# Revit family: bfs-300_1000tx2_50Hz
name_source: partatom
category: 機械設備
units: mm (PartAtom-declared; Revit-internal decimal feet)

## family parameters
OmniClass タイトル = Axial Fans
OmniClass 番号 = 23.75.35.17.24
パーツ タイプ = 割り込み
ロード時にボイドで切り取り = いいえ
丸型コネクタ寸法 = 直径を使用
作業面ベース = いいえ
共有 = いいえ
常に垂直 = はい
部屋計算ポイント = はい

## types (5) — shared parameters
IfcExportAs = IfcFanType
IfcExportType = CENTRIFUGALFORWARDCURVED
M = 80  [stored 0.262467 ft]
MID静圧 = 0.0 Pa
MID風量 = 0.0 m³/h
MIN静圧 = 0.0 Pa
MIN風量 = 0.0 m³/h
OmniClassCode = 23-33 31 19 13 15
URL = https://www.mitsubishielectric.co.jp
Uniclass2015Code = Pr_65_67_29_12
Uniclass2015Title = Centrifugal fans
Uniclass2015Version = Systems v1.9
サービススペース = はい
ドレン管径 = 18 mm
ファンの種類 = 多翼形
仕様書バージョン = Version1.0
企業コード = 108420
分類コード = 50052502100020
周波数 = 50 Hz
呼称 = 消音ボックス付送風機
実風量 = 0.0 m³/h
形名 = BFS-TX : BFS-300TX
本体マテリアル = SUS304
極 = 4
極数 = 3
法定耐用年数 = 15
盤工事区分 = 電気工事
相 = 3
積算_科目 = 2 換気設備
製品リリース年月 = 2022年6月1日
製品出荷対象 = 国内
製造元 = 三菱電機株式会社
設置方法 = 天吊
説明 = ストレートシロッコファン厨房用
負荷分類 = 3_ファン類
運転質量 = 0.00 kg
電圧 = 200 V
zero-valued in all types: Clearance Bottom, Clearance Right, Clearance Top

## per-type parameters (varying)
| type | Clearance Back | Clearance Front | Clearance Left | Depth | Front-d | Height | MAX静圧 | MAX風量 | Width | ダクト幅 | ダクト高 | 価格 | 天吊金具ピッチ奥行 | 天吊金具ピッチ幅 | 消費電力 | 番手 | 製品質量 | 質量 | 電動機出力 | 騒音レベル(dB(A)) | 騒音レベル(dB(A))_側面 | 騒音レベル(dB(A))_吐出 | 騒音レベル(dB(A))_吸込 |
| BFS-300TX2 | 0  [stored 0 ft] | 0  [stored 0 ft] | 600  [stored 1.9685 ft] | 614  [stored 2.01444 ft] | 80  [stored 0.262467 ft] | 411  [stored 1.34843 ft] | 200.0 Pa | 3000.0 m³/h | 546  [stored 1.79134 ft] | 300 mm | 300 mm | 463000 $ | 562  [stored 1.84383 ft] | 655  [stored 2.14895 ft] | 940 W | #2 | 39.00 kg | 46.80 kg | 1500 W | 68 | 49 | 73 | 68 |
| BFS-450TX2 | 600  [stored 1.9685 ft] | 600  [stored 1.9685 ft] | 1200 | 728  [stored 2.38845 ft] | 81.5  [stored 0.267388 ft] | 415  [stored 1.36155 ft] | 190.0 Pa | 4500.0 m³/h | 819  [stored 2.68701 ft] | 700 mm | 250 mm | 745000 $ | 685 | 922  [stored 3.02493 ft] | 1030 W | #1 1/2×2 | 77.00 kg | 92.40 kg | 2200 W | 63 | 46 | 71 | 63 |
| BFS-550TX2 | 600  [stored 1.9685 ft] | 600  [stored 1.9685 ft] | 1200 | 771  [stored 2.52953 ft] | 81.5  [stored 0.267388 ft] | 455 | 200.0 Pa | 5500.0 m³/h | 912  [stored 2.99213 ft] | 750 mm | 300 mm | 830000 $ | 728  [stored 2.38845 ft] | 1015  [stored 3.33005 ft] | 1660 W | #2×2 | 84.00 kg | 100.80 kg | 3000 W | 68 | 49 | 71 | 68 |
| BFS-800TX2 | 18  [stored 0.0590551 ft] | 18  [stored 0.0590551 ft] | 1100 | 1690  [stored 5.54462 ft] | 18  [stored 0.0590551 ft] | 461.4  [stored 1.51378 ft] | 200.0 Pa | 8000.0 m³/h | 952  [stored 3.12336 ft] | 800 mm | 300 mm | 1980000 $ | 1630  [stored 5.34777 ft] | 1018  [stored 3.3399 ft] | 2600 W | #2×3 | 121.00 kg | 145.20 kg | 3500 W | 68 | 48.5 | 70.5 | 68 |
| BFS-1000TX2 | 18  [stored 0.0590551 ft] | 18  [stored 0.0590551 ft] | 1100 | 1910  [stored 6.2664 ft] | 18  [stored 0.0590551 ft] | 461.4  [stored 1.51378 ft] | 205.0 Pa | 10000.0 m³/h | 1072 | 900 mm | 300 mm | 2338000 $ | 1850  [stored 6.06955 ft] | 1138  [stored 3.7336 ft] | 3350 W | #2×4 | 152.00 kg | 182.40 kg | 4400 W | 68.5 | 49 | 71 | 68.5 |

note: column(s) folded — value = type name in every type: モデル

note: [stored X ft] marks values corroborated as IEEE doubles in the binary element streams (Revit-internal decimal feet)
